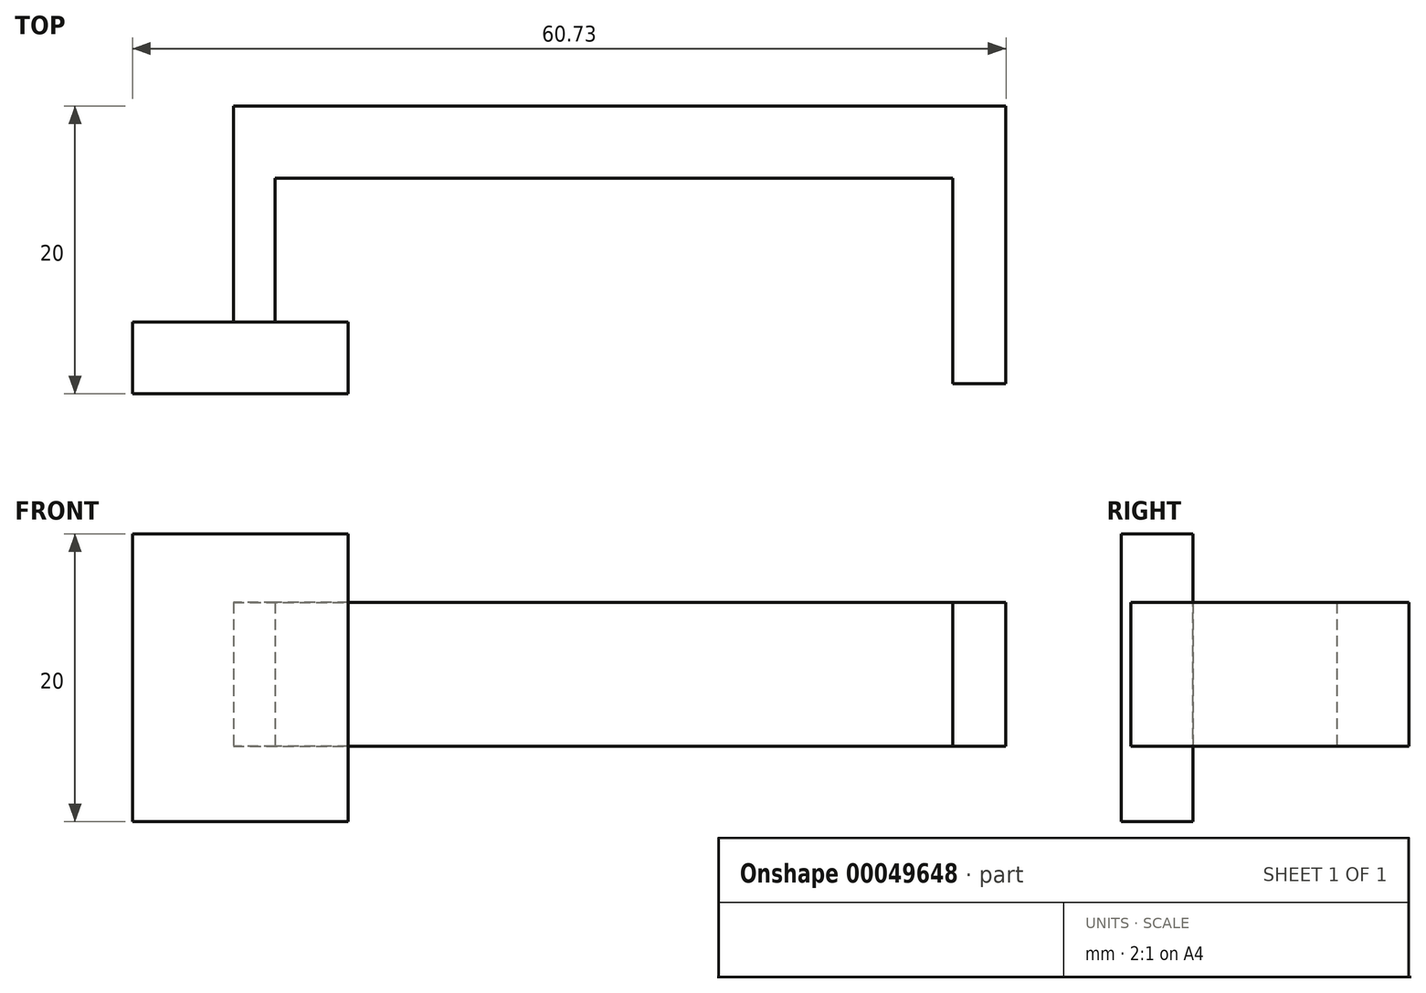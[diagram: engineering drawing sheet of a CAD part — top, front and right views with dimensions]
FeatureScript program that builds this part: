
annotation { "Feature Type Name" : "Feature", "Feature Type Description" : "" }
export const myFeature = defineFeature(function(context is Context, id is Id, definition is map)
    precondition{}
    {
        {
            var Q0;
            Q0=qCreatedBy(makeId("Front.planeOp"),FACE);
            var sketch = newSketch(context, id + "F0", { "sketchPlane" : qUnion([Q0])});
            skLineSegment(sketch, "E0.left", {"start": v(0, 0) * mm, "end": v(0, 9.77) * mm});
            skLineSegment(sketch, "E1.bottom", {"start": v(0, 9.77) * mm, "end": v(15, 9.77) * mm});
            skLineSegment(sketch, "E1.top", {"start": v(0, -10.23) * mm, "end": v(15, -10.23) * mm});
            skLineSegment(sketch, "E1.left", {"start": v(0, 9.77) * mm, "end": v(0, -10.23) * mm});
            skLineSegment(sketch, "E1.right", {"start": v(15, 9.77) * mm, "end": v(15, -10.23) * mm});
            skSolve(sketch);
        }
        {
            var Q0;
            Q0=makeQuery(id+"F0.imprint","IMPRINT",FACE,{"disambiguationData":[TD([[makeQuery(id+"F0.imprint","IMPRINT",EDGE,{"derivedFrom":sQuery(id+"F0.wireOp",EDGE,"E0.bottom")}),1.0]])]});
            var Q1;
            {var subQ0=sQuery(id+"F0.wireOp",EDGE,"E1.bottom");Q1=makeQuery(id+"F0.imprint","IMPRINT",FACE,{"disambiguationData":[TD([[makeQuery(id+"F0.imprint","IMPRINT",EDGE,{"derivedFrom":subQ0}),-1.0]])]});}
            extrude(context, id + "F1", {"entities" : qUnion([Q0, Q1]), "depth" : 5 * mm});
        }
        {
            var Q0;
            Q0=qCreatedBy(makeId("Top.planeOp"),FACE);
            var sketch = newSketch(context, id + "F2", { "sketchPlane" : qUnion([Q0])});
            skLineSegment(sketch, "E2", {"start": v(7.02, 0) * mm, "end": v(7.02, 15) * mm});
            skLineSegment(sketch, "E3", {"start": v(7.02, 15) * mm, "end": v(60.73, 15) * mm});
            skLineSegment(sketch, "E4", {"start": v(60.73, 15) * mm, "end": v(60.73, -4.3) * mm});
            skLineSegment(sketch, "E5", {"start": v(60.73, -4.3) * mm, "end": v(57.02, -4.3) * mm});
            skLineSegment(sketch, "E6", {"start": v(57.02, -4.3) * mm, "end": v(57.02, 10) * mm});
            skLineSegment(sketch, "E7", {"start": v(57.02, 10) * mm, "end": v(9.9, 10) * mm});
            skLineSegment(sketch, "E8", {"start": v(9.9, 10) * mm, "end": v(9.9, 0) * mm});
            skLineSegment(sketch, "E9", {"start": v(9.9, 0) * mm, "end": v(7.02, 0) * mm});
            skSolve(sketch);
        }
        {
            var Q0;
            Q0 = qSketchRegion(id + "F2", true);
            extrude(context, id + "F3", {"entities" : qUnion([Q0]), "operationType" : NewBodyOperationType.ADD, "depth" : 5 * mm, "hasSecondDirection" : true, "secondDirectionOppositeDirection" : true, "secondDirectionDepth" : 5 * mm});
        }
    });
